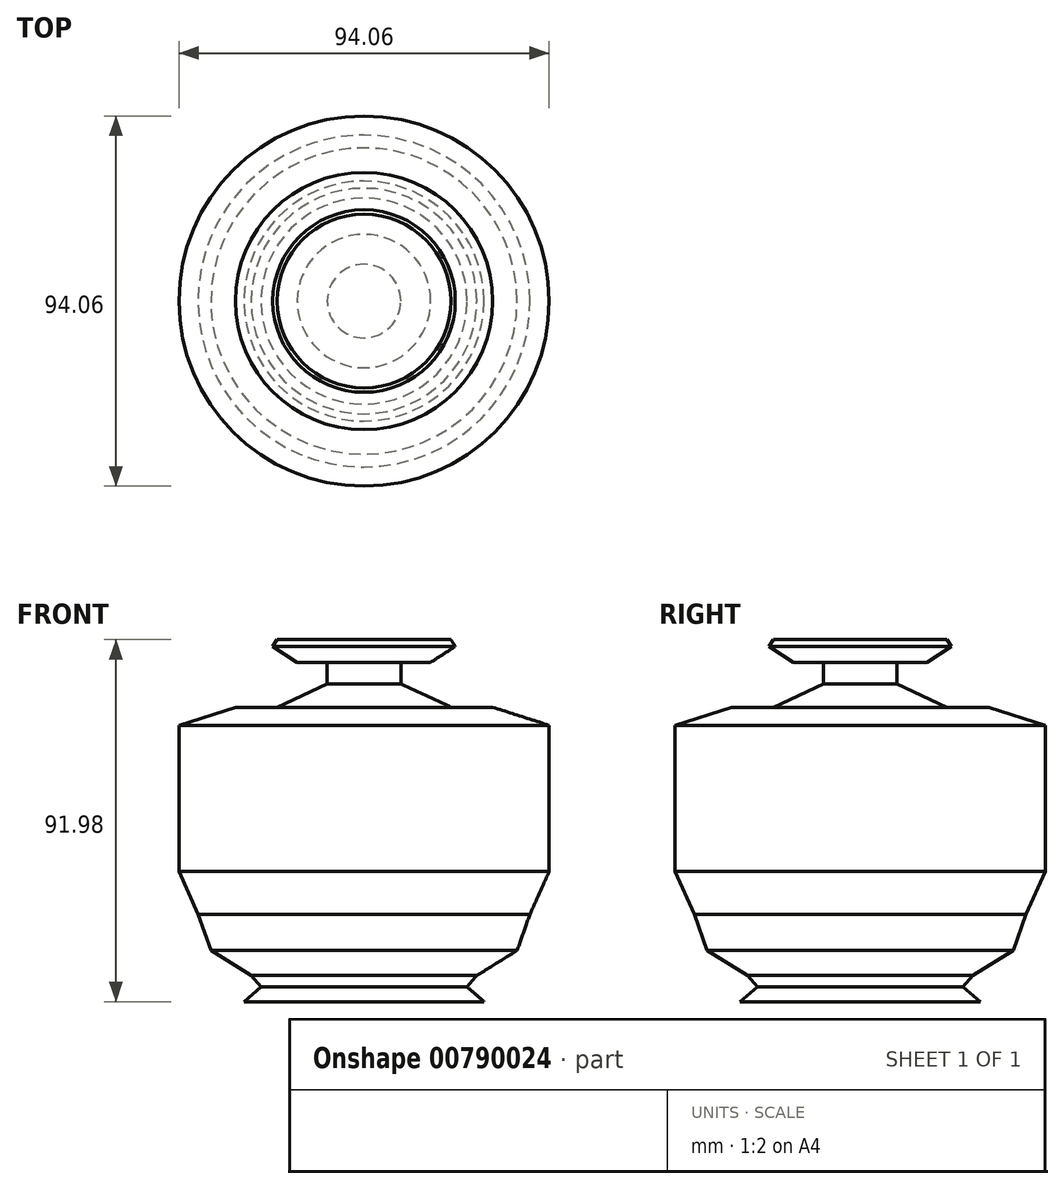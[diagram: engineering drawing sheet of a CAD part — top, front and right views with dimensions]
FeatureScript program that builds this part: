
annotation { "Feature Type Name" : "Feature", "Feature Type Description" : "" }
export const myFeature = defineFeature(function(context is Context, id is Id, definition is map)
    precondition{}
    {
        {
            var Q0;
            Q0=qCreatedBy(makeId("Front.planeOp"),FACE);
            var sketch = newSketch(context, id + "F0", { "sketchPlane" : qUnion([Q0])});
            skLineSegment(sketch, "E0", {"start": v(0, -41.61) * mm, "end": v(30.5, -41.61) * mm});
            skLineSegment(sketch, "E1", {"start": v(30.5, -41.61) * mm, "end": v(26.16, -37.82) * mm});
            skLineSegment(sketch, "E2", {"start": v(26.16, -37.82) * mm, "end": v(28.66, -34.96) * mm});
            skLineSegment(sketch, "E3", {"start": v(28.66, -34.96) * mm, "end": v(38.9, -28.6) * mm});
            skLineSegment(sketch, "E4", {"start": v(38.9, -28.6) * mm, "end": v(42.15, -19.38) * mm});
            skLineSegment(sketch, "E5", {"start": v(42.15, -19.38) * mm, "end": v(47.03, -8.54) * mm});
            skLineSegment(sketch, "E6", {"start": v(47.03, -8.54) * mm, "end": v(47.03, 11.8) * mm});
            skLineSegment(sketch, "E7", {"start": v(47.03, 11.8) * mm, "end": v(47.03, 28.6) * mm});
            skLineSegment(sketch, "E8", {"start": v(47.03, 28.6) * mm, "end": v(32.67, 33.2) * mm});
            skLineSegment(sketch, "E9", {"start": v(32.67, 33.2) * mm, "end": v(22.1, 33.2) * mm});
            skLineSegment(sketch, "E10", {"start": v(22.1, 33.2) * mm, "end": v(9.35, 39.17) * mm});
            skLineSegment(sketch, "E11", {"start": v(9.35, 39.17) * mm, "end": v(9.35, 44.6) * mm});
            skLineSegment(sketch, "E12", {"start": v(9.35, 44.6) * mm, "end": v(16.94, 44.6) * mm});
            skLineSegment(sketch, "E13", {"start": v(16.94, 44.6) * mm, "end": v(23.18, 48.66) * mm});
            skLineSegment(sketch, "E14", {"start": v(23.18, 48.66) * mm, "end": v(22.06, 50.37) * mm});
            skLineSegment(sketch, "E15", {"start": v(22.06, 50.37) * mm, "end": v(9.62, 50.37) * mm});
            skLineSegment(sketch, "E16", {"start": v(9.62, 50.37) * mm, "end": v(0, 50.37) * mm});
            skLineSegment(sketch, "E17", {"start": v(0, 50.37) * mm, "end": v(0, -41.61) * mm});
            skLineSegment(sketch, "E18", {"start": v(0, 95.01) * mm, "end": v(0, -99.62) * mm, "construction": true});
            skSolve(sketch);
        }
        {
            var Q0;
            Q0=makeQuery(id+"F0.imprint","IMPRINT",FACE,{"disambiguationData":[TD([[makeQuery(id+"F0.imprint","IMPRINT",EDGE,{"derivedFrom":sQuery(id+"F0.wireOp",EDGE,"E0")}),1.0]])]});
            var Q1;
            Q1=sQuery(id+"F0.wireOp",EDGE,"E18");
            revolve(context, id + "F1", {"surfaceOperationType" : NewSurfaceOperationType.NEW, "entities" : qUnion([Q0]), "axis" : qUnion([Q1]), "revolveType" : RevolveType.FULL});
        }
    });
